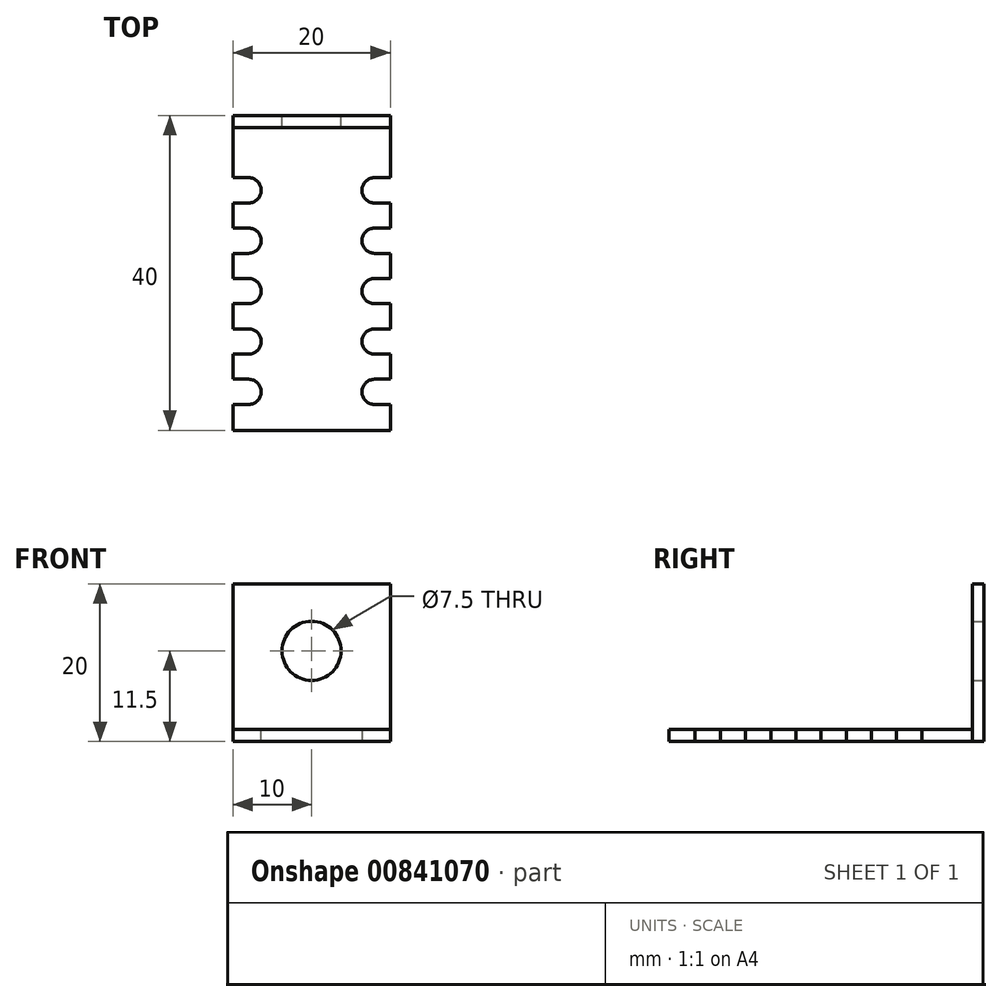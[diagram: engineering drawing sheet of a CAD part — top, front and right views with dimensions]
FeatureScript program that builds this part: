
annotation { "Feature Type Name" : "Feature", "Feature Type Description" : "" }
export const myFeature = defineFeature(function(context is Context, id is Id, definition is map)
    precondition{}
    {
        {
            var Q0;
            Q0=qCreatedBy(makeId("Top.planeOp"),FACE);
            var sketch = newSketch(context, id + "F0", { "sketchPlane" : qUnion([Q0])});
            skLineSegment(sketch, "E0.bottom", {"start": v(0, 0) * mm, "end": v(20, 0) * mm});
            skLineSegment(sketch, "E0.top", {"start": v(0, 40) * mm, "end": v(20, 40) * mm});
            skLineSegment(sketch, "E0.left", {"start": v(0, 0) * mm, "end": v(0, 40) * mm});
            skLineSegment(sketch, "E0.right", {"start": v(20, 0) * mm, "end": v(20, 40) * mm});
            skLineSegment(sketch, "E1.bottom", {"start": v(20, 32.1) * mm, "end": v(16.4, 32.1) * mm});
            skLineSegment(sketch, "E1.top", {"start": v(20, 28.9) * mm, "end": v(16.4, 28.9) * mm});
            skLineSegment(sketch, "E1.left", {"start": v(20, 32.1) * mm, "end": v(20, 28.9) * mm});
            skLineSegment(sketch, "E1.right", {"start": v(16.4, 32.1) * mm, "end": v(16.4, 28.9) * mm});
            skLineSegment(sketch, "E2", {"start": v(3.12, 30.5) * mm, "end": v(18, 30.5) * mm, "construction": true});
            skLineSegment(sketch, "E3.bottom", {"start": v(20, 25.7) * mm, "end": v(16.4, 25.7) * mm});
            skLineSegment(sketch, "E3.top", {"start": v(20, 22.5) * mm, "end": v(16.4, 22.5) * mm});
            skLineSegment(sketch, "E3.left", {"start": v(20, 25.7) * mm, "end": v(20, 22.5) * mm});
            skLineSegment(sketch, "E3.right", {"start": v(16.4, 25.7) * mm, "end": v(16.4, 22.5) * mm});
            skLineSegment(sketch, "E4.bottom", {"start": v(20, 19.3) * mm, "end": v(16.4, 19.3) * mm});
            skLineSegment(sketch, "E4.top", {"start": v(20, 16.1) * mm, "end": v(16.4, 16.1) * mm});
            skLineSegment(sketch, "E4.left", {"start": v(20, 19.3) * mm, "end": v(20, 16.1) * mm});
            skLineSegment(sketch, "E4.right", {"start": v(16.4, 19.3) * mm, "end": v(16.4, 16.1) * mm});
            skLineSegment(sketch, "E5.bottom", {"start": v(20, 12.9) * mm, "end": v(16.4, 12.9) * mm});
            skLineSegment(sketch, "E5.top", {"start": v(20, 9.7) * mm, "end": v(16.4, 9.7) * mm});
            skLineSegment(sketch, "E5.left", {"start": v(20, 12.9) * mm, "end": v(20, 9.7) * mm});
            skLineSegment(sketch, "E5.right", {"start": v(16.4, 12.9) * mm, "end": v(16.4, 9.7) * mm});
            skLineSegment(sketch, "E6.bottom", {"start": v(20, 6.5) * mm, "end": v(16.4, 6.5) * mm});
            skLineSegment(sketch, "E6.top", {"start": v(20, 3.3) * mm, "end": v(16.4, 3.3) * mm});
            skLineSegment(sketch, "E6.left", {"start": v(20, 6.5) * mm, "end": v(20, 3.3) * mm});
            skLineSegment(sketch, "E6.right", {"start": v(16.4, 6.5) * mm, "end": v(16.4, 3.3) * mm});
            skLineSegment(sketch, "E7.bottom", {"start": v(0, 32.1) * mm, "end": v(3.6, 32.1) * mm});
            skLineSegment(sketch, "E7.top", {"start": v(0, 28.9) * mm, "end": v(3.6, 28.9) * mm});
            skLineSegment(sketch, "E7.left", {"start": v(0, 32.1) * mm, "end": v(0, 28.9) * mm});
            skLineSegment(sketch, "E7.right", {"start": v(3.6, 32.1) * mm, "end": v(3.6, 28.9) * mm});
            skLineSegment(sketch, "E8.bottom", {"start": v(0, 25.7) * mm, "end": v(3.6, 25.7) * mm});
            skLineSegment(sketch, "E8.top", {"start": v(0, 22.5) * mm, "end": v(3.6, 22.5) * mm});
            skLineSegment(sketch, "E8.left", {"start": v(0, 25.7) * mm, "end": v(0, 22.5) * mm});
            skLineSegment(sketch, "E8.right", {"start": v(3.6, 25.7) * mm, "end": v(3.6, 22.5) * mm});
            skLineSegment(sketch, "E9.bottom", {"start": v(0, 12.9) * mm, "end": v(3.6, 12.9) * mm});
            skLineSegment(sketch, "E9.top", {"start": v(0, 9.7) * mm, "end": v(3.6, 9.7) * mm});
            skLineSegment(sketch, "E9.left", {"start": v(0, 12.9) * mm, "end": v(0, 9.7) * mm});
            skLineSegment(sketch, "E9.right", {"start": v(3.6, 12.9) * mm, "end": v(3.6, 9.7) * mm});
            skLineSegment(sketch, "E10.bottom", {"start": v(0, 6.5) * mm, "end": v(3.6, 6.5) * mm});
            skLineSegment(sketch, "E10.top", {"start": v(0, 3.3) * mm, "end": v(3.6, 3.3) * mm});
            skLineSegment(sketch, "E10.left", {"start": v(0, 6.5) * mm, "end": v(0, 3.3) * mm});
            skLineSegment(sketch, "E10.right", {"start": v(3.6, 6.5) * mm, "end": v(3.6, 3.3) * mm});
            skLineSegment(sketch, "E11.bottom", {"start": v(0, 19.3) * mm, "end": v(3.6, 19.3) * mm});
            skLineSegment(sketch, "E11.top", {"start": v(0, 16.1) * mm, "end": v(3.6, 16.1) * mm});
            skLineSegment(sketch, "E11.left", {"start": v(0, 19.3) * mm, "end": v(0, 16.1) * mm});
            skLineSegment(sketch, "E11.right", {"start": v(3.6, 19.3) * mm, "end": v(3.6, 16.1) * mm});
            skLineSegment(sketch, "E12.top", {"start": v(0, 38.5) * mm, "end": v(20, 38.5) * mm});
            skLineSegment(sketch, "E12.left", {"start": v(0, 40) * mm, "end": v(0, 38.5) * mm});
            skLineSegment(sketch, "E12.right", {"start": v(20, 40) * mm, "end": v(20, 38.5) * mm});
            skSolve(sketch);
        }
        {
            var Q0;
            {var subQ8=sQuery(id+"F0.wireOp",EDGE,"E0.bottom");Q0=makeQuery(id+"F0.imprint","IMPRINT",FACE,{"disambiguationData":[TD([[makeQuery(id+"F0.imprint","IMPRINT",EDGE,{"derivedFrom":subQ8}),1.0]])]});}
            extrude(context, id + "F1", {"entities" : qUnion([Q0]), "depth" : 1.5 * mm, "offsetDistance" : 25 * mm});
        }
        {
            var Q0;
            Q0=makeQuery(id+"F0.imprint","IMPRINT",FACE,{"disambiguationData":[TD([[makeQuery(id+"F0.imprint","IMPRINT",EDGE,{"derivedFrom":sQuery(id+"F0.wireOp",EDGE,"E0.top")}),-1.0]])]});
            extrude(context, id + "F2", {"entities" : qUnion([Q0]), "depth" : 20 * mm, "offsetDistance" : 25 * mm});
        }
        {
            var Q0;
            Q0=makeQuery(id+"F2.opExtrude","SWEPT_FACE",FACE,{"disambiguationData":[OSD([sQuery(id+"F0.wireOp",EDGE,"E0.top")])]});
            var sketch = newSketch(context, id + "F3", { "sketchPlane" : qUnion([Q0])});
            skCircle(sketch, "E13", {"center": v(-10, 11.5) * mm, "radius": 3.75 * mm});
            skSolve(sketch);
        }
        {
            var Q0;
            Q0=makeQuery(id+"F3.imprint","IMPRINT",FACE,{"disambiguationData":[TD([[makeQuery(id+"F3.imprint","IMPRINT",EDGE,{"derivedFrom":sQuery(id+"F3.wireOp",EDGE,"E13")}),1.0]])]});
            extrude(context, id + "F4", {"entities" : qUnion([Q0]), "operationType" : NewBodyOperationType.REMOVE, "oppositeDirection" : true, "depth" : 25 * mm, "offsetDistance" : 25 * mm});
        }
        {
            var Q0;
            Q0=makeQuery(id+"F1.opExtrude","SWEPT_EDGE",EDGE,{"disambiguationData":[OSD([sQuery(id+"F0.wireOp",EDGE,"E1.bottom"),sQuery(id+"F0.wireOp",EDGE,"E1.right")])]});
            var Q1;
            Q1=makeQuery(id+"F1.opExtrude","SWEPT_EDGE",EDGE,{"disambiguationData":[OSD([sQuery(id+"F0.wireOp",EDGE,"E1.top"),sQuery(id+"F0.wireOp",EDGE,"E1.right")])]});
            var Q2;
            Q2=makeQuery(id+"F1.opExtrude","SWEPT_EDGE",EDGE,{"disambiguationData":[OSD([sQuery(id+"F0.wireOp",EDGE,"E3.bottom"),sQuery(id+"F0.wireOp",EDGE,"E3.right")])]});
            var Q3;
            Q3=makeQuery(id+"F1.opExtrude","SWEPT_EDGE",EDGE,{"disambiguationData":[OSD([sQuery(id+"F0.wireOp",EDGE,"E3.top"),sQuery(id+"F0.wireOp",EDGE,"E3.right")])]});
            var Q4;
            Q4=makeQuery(id+"F1.opExtrude","SWEPT_EDGE",EDGE,{"disambiguationData":[OSD([sQuery(id+"F0.wireOp",EDGE,"E4.top"),sQuery(id+"F0.wireOp",EDGE,"E4.right")])]});
            var Q5;
            Q5=makeQuery(id+"F1.opExtrude","SWEPT_EDGE",EDGE,{"disambiguationData":[OSD([sQuery(id+"F0.wireOp",EDGE,"E5.top"),sQuery(id+"F0.wireOp",EDGE,"E5.right")])]});
            var Q6;
            Q6=makeQuery(id+"F1.opExtrude","SWEPT_EDGE",EDGE,{"disambiguationData":[OSD([sQuery(id+"F0.wireOp",EDGE,"E6.top"),sQuery(id+"F0.wireOp",EDGE,"E6.right")])]});
            var Q7;
            Q7=makeQuery(id+"F1.opExtrude","SWEPT_EDGE",EDGE,{"disambiguationData":[OSD([sQuery(id+"F0.wireOp",EDGE,"E4.bottom"),sQuery(id+"F0.wireOp",EDGE,"E4.right")])]});
            var Q8;
            Q8=makeQuery(id+"F1.opExtrude","SWEPT_EDGE",EDGE,{"disambiguationData":[OSD([sQuery(id+"F0.wireOp",EDGE,"E5.bottom"),sQuery(id+"F0.wireOp",EDGE,"E5.right")])]});
            var Q9;
            Q9=makeQuery(id+"F1.opExtrude","SWEPT_EDGE",EDGE,{"disambiguationData":[OSD([sQuery(id+"F0.wireOp",EDGE,"E6.bottom"),sQuery(id+"F0.wireOp",EDGE,"E6.right")])]});
            var Q10;
            Q10=makeQuery(id+"F1.opExtrude","SWEPT_EDGE",EDGE,{"disambiguationData":[OSD([sQuery(id+"F0.wireOp",EDGE,"E7.bottom"),sQuery(id+"F0.wireOp",EDGE,"E7.right")])]});
            var Q11;
            Q11=makeQuery(id+"F1.opExtrude","SWEPT_EDGE",EDGE,{"disambiguationData":[OSD([sQuery(id+"F0.wireOp",EDGE,"E8.bottom"),sQuery(id+"F0.wireOp",EDGE,"E8.right")])]});
            var Q12;
            Q12=makeQuery(id+"F1.opExtrude","SWEPT_EDGE",EDGE,{"disambiguationData":[OSD([sQuery(id+"F0.wireOp",EDGE,"E11.bottom"),sQuery(id+"F0.wireOp",EDGE,"E11.right")])]});
            var Q13;
            Q13=makeQuery(id+"F1.opExtrude","SWEPT_EDGE",EDGE,{"disambiguationData":[OSD([sQuery(id+"F0.wireOp",EDGE,"E9.bottom"),sQuery(id+"F0.wireOp",EDGE,"E9.right")])]});
            var Q14;
            Q14=makeQuery(id+"F1.opExtrude","SWEPT_EDGE",EDGE,{"disambiguationData":[OSD([sQuery(id+"F0.wireOp",EDGE,"E10.bottom"),sQuery(id+"F0.wireOp",EDGE,"E10.right")])]});
            var Q15;
            Q15=makeQuery(id+"F1.opExtrude","SWEPT_EDGE",EDGE,{"disambiguationData":[OSD([sQuery(id+"F0.wireOp",EDGE,"E7.top"),sQuery(id+"F0.wireOp",EDGE,"E7.right")])]});
            var Q16;
            Q16=makeQuery(id+"F1.opExtrude","SWEPT_EDGE",EDGE,{"disambiguationData":[OSD([sQuery(id+"F0.wireOp",EDGE,"E8.top"),sQuery(id+"F0.wireOp",EDGE,"E8.right")])]});
            var Q17;
            Q17=makeQuery(id+"F1.opExtrude","SWEPT_EDGE",EDGE,{"disambiguationData":[OSD([sQuery(id+"F0.wireOp",EDGE,"E11.top"),sQuery(id+"F0.wireOp",EDGE,"E11.right")])]});
            var Q18;
            Q18=makeQuery(id+"F1.opExtrude","SWEPT_EDGE",EDGE,{"disambiguationData":[OSD([sQuery(id+"F0.wireOp",EDGE,"E9.top"),sQuery(id+"F0.wireOp",EDGE,"E9.right")])]});
            var Q19;
            Q19=makeQuery(id+"F1.opExtrude","SWEPT_EDGE",EDGE,{"disambiguationData":[OSD([sQuery(id+"F0.wireOp",EDGE,"E10.top"),sQuery(id+"F0.wireOp",EDGE,"E10.right")])]});
            fillet(context, id + "F5", {"entities" : qUnion([Q0, Q1, Q2, Q3, Q4, Q5, Q6, Q7, Q8, Q9, Q10, Q11, Q12, Q13, Q14, Q15, Q16, Q17, Q18, Q19]), "radius" : 1.6 * mm, "tangentPropagation" : true, "allowEdgeOverflow" : false});
        }
    });
